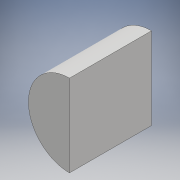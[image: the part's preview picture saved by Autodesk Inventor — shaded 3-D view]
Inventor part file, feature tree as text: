
AUTODESK INVENTOR PART (.ipt)
format: ipt  version: 2018 (Build 220112000, 112)  size: 88,064 bytes
history: native  units: mm
features: extrude x1, sketch x1
ambient origin geometry x8: Origin, YZ Plane, XZ Plane, XY Plane, X Axis, Y Axis, Z Axis, Center Point
bodies: Solid1 (feature_tree)
feature tree (2):
  extrude  "Extrusion1"  Depth=10.0mm TaperAngle=0.0deg
  sketch  "Sketch1"  dims[d0=10.0mm d1=10.0mm d2=0.0mm]
